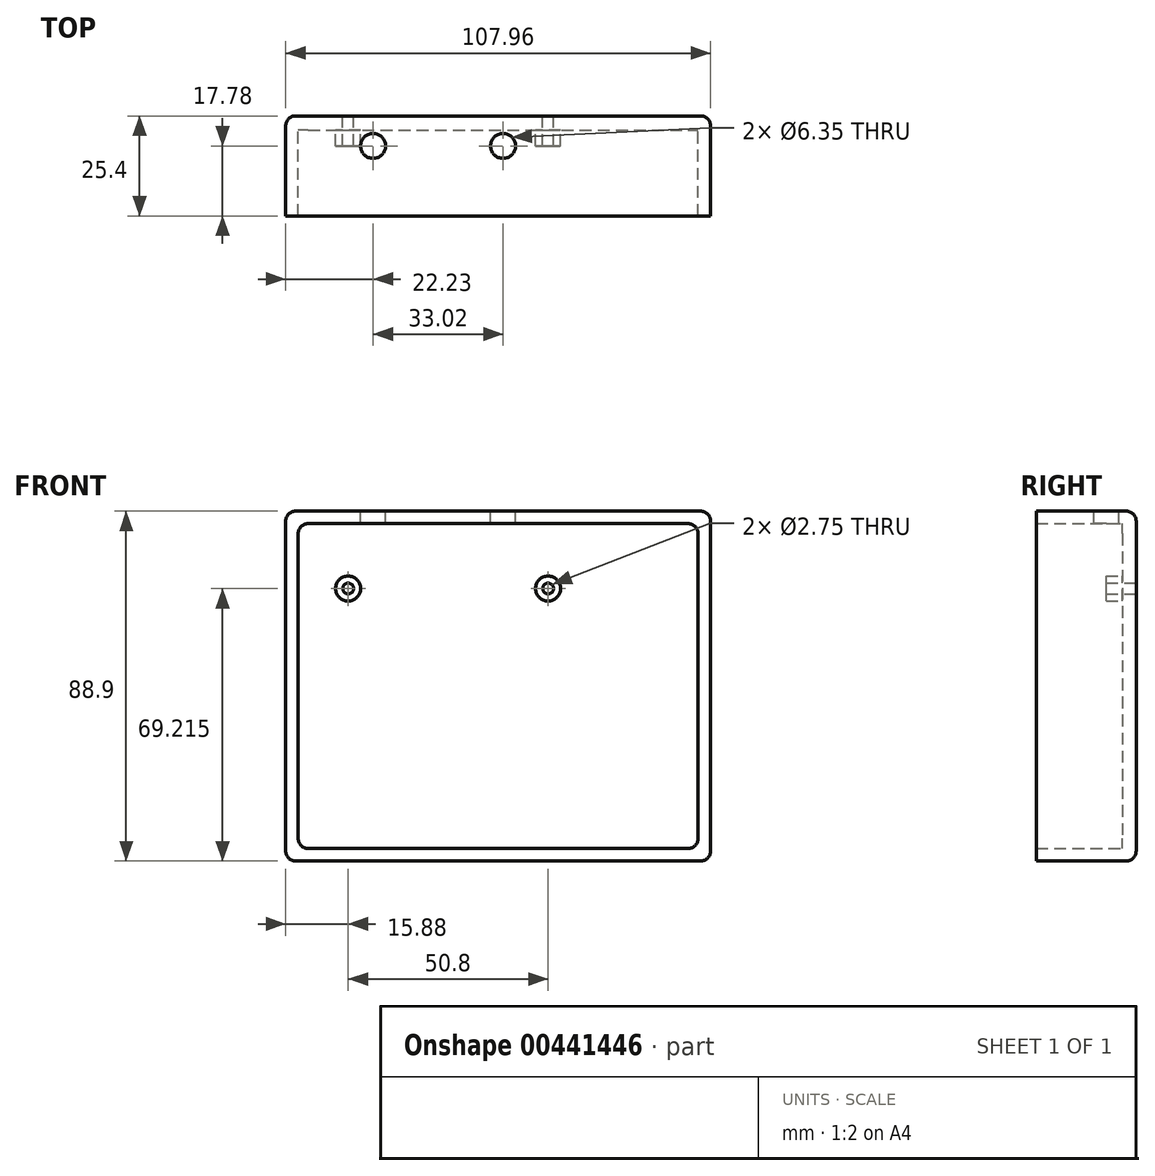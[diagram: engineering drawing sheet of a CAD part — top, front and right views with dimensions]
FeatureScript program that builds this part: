
annotation { "Feature Type Name" : "Feature", "Feature Type Description" : "" }
export const myFeature = defineFeature(function(context is Context, id is Id, definition is map)
    precondition{}
    {
        {
            var Q0;
            Q0=qCreatedBy(makeId("Front.planeOp"),FACE);
            var sketch = newSketch(context, id + "F0", { "sketchPlane" : qUnion([Q0])});
            skLineSegment(sketch, "E0.bottom", {"start": v(50.8, -41.27) * mm, "end": v(-50.8, -41.28) * mm});
            skLineSegment(sketch, "E0.top", {"start": v(50.8, 41.28) * mm, "end": v(-50.8, 41.27) * mm});
            skLineSegment(sketch, "E0.left", {"start": v(50.8, -41.27) * mm, "end": v(50.8, 41.28) * mm});
            skLineSegment(sketch, "E0.right", {"start": v(-50.8, -41.28) * mm, "end": v(-50.8, 41.27) * mm});
            skPoint(sketch, "E0.middle", {"position": v(0, 0) * mm});
            skCircle(sketch, "E1", {"center": v(-38.1, 24.77) * mm, "radius": 3.18 * mm});
            skCircle(sketch, "E2", {"center": v(-38.1, 24.77) * mm, "radius": 1.38 * mm});
            skCircle(sketch, "E3", {"center": v(12.7, 24.77) * mm, "radius": 3.18 * mm});
            skCircle(sketch, "E4", {"center": v(12.7, 24.77) * mm, "radius": 1.38 * mm});
            skLineSegment(sketch, "E5.bottom", {"start": v(53.98, -44.45) * mm, "end": v(-53.98, -44.45) * mm});
            skLineSegment(sketch, "E5.top", {"start": v(53.98, 44.45) * mm, "end": v(-53.98, 44.45) * mm});
            skLineSegment(sketch, "E5.left", {"start": v(53.98, -44.45) * mm, "end": v(53.98, 44.45) * mm});
            skLineSegment(sketch, "E5.right", {"start": v(-53.98, -44.45) * mm, "end": v(-53.98, 44.45) * mm});
            skSolve(sketch);
        }
        {
            var Q0;
            Q0=makeQuery(id+"F0.imprint","IMPRINT",FACE,{"disambiguationData":[TD([[makeQuery(id+"F0.imprint","IMPRINT",EDGE,{"derivedFrom":sQuery(id+"F0.wireOp",EDGE,"E0.bottom")}),1.0]])]});
            var Q1;
            Q1=makeQuery(id+"F0.imprint","IMPRINT",FACE,{"disambiguationData":[TD([[makeQuery(id+"F0.imprint","IMPRINT",EDGE,{"derivedFrom":sQuery(id+"F0.wireOp",EDGE,"E0.bottom")}),-1.0]])]});
            extrude(context, id + "F1", {"entities" : qUnion([Q0, Q1]), "depth" : 3.56 * mm});
        }
        {
            var Q0;
            Q0=makeQuery(id+"F0.imprint","IMPRINT",FACE,{"disambiguationData":[TD([[makeQuery(id+"F0.imprint","IMPRINT",EDGE,{"derivedFrom":sQuery(id+"F0.wireOp",EDGE,"E1")}),1.0]])]});
            var Q1;
            Q1=makeQuery(id+"F0.imprint","IMPRINT",FACE,{"disambiguationData":[TD([[makeQuery(id+"F0.imprint","IMPRINT",EDGE,{"derivedFrom":sQuery(id+"F0.wireOp",EDGE,"E3")}),1.0]])]});
            extrude(context, id + "F2", {"entities" : qUnion([Q0, Q1]), "operationType" : NewBodyOperationType.ADD, "depth" : 7.62 * mm});
        }
        {
            var Q0;
            Q0=makeQuery(id+"F0.imprint","IMPRINT",FACE,{"disambiguationData":[TD([[makeQuery(id+"F0.imprint","IMPRINT",EDGE,{"derivedFrom":sQuery(id+"F0.wireOp",EDGE,"E0.bottom")}),1.0]])]});
            extrude(context, id + "F3", {"entities" : qUnion([Q0]), "operationType" : NewBodyOperationType.ADD, "depth" : 25.4 * mm});
        }
        {
            var Q0;
            {var subQ0=sQuery(id+"F0.wireOp",EDGE,"E5.top");Q0=makeQuery(id+"F3.boolean.opBoolean","MERGE",FACE,{"derivedFrom":[makeQuery(id+"F1.opExtrude","SWEPT_FACE",FACE,{"disambiguationData":[OSD([subQ0])]}),makeQuery(id+"F3.opExtrude","SWEPT_FACE",FACE,{"disambiguationData":[OSD([subQ0])]})]});}
            var sketch = newSketch(context, id + "F4", { "sketchPlane" : qUnion([Q0])});
            skCircle(sketch, "E6", {"center": v(-31.75, -7.62) * mm, "radius": 3.18 * mm});
            skCircle(sketch, "E7", {"center": v(1.27, -7.62) * mm, "radius": 3.18 * mm});
            skSolve(sketch);
        }
        {
            var Q0;
            Q0=makeQuery(id+"F4.imprint","IMPRINT",FACE,{"disambiguationData":[TD([[makeQuery(id+"F4.imprint","IMPRINT",EDGE,{"derivedFrom":sQuery(id+"F4.wireOp",EDGE,"E7")}),1.0]])]});
            var Q1;
            Q1=makeQuery(id+"F4.imprint","IMPRINT",FACE,{"disambiguationData":[TD([[makeQuery(id+"F4.imprint","IMPRINT",EDGE,{"derivedFrom":sQuery(id+"F4.wireOp",EDGE,"E6")}),1.0]])]});
            extrude(context, id + "F5", {"entities" : qUnion([Q0, Q1]), "operationType" : NewBodyOperationType.REMOVE, "oppositeDirection" : true, "depth" : 5.08 * mm});
        }
        {
            var Q0;
            {var subQ0=sQuery(id+"F0.wireOp",EDGE,"E5.right");var subQ1=sQuery(id+"F0.wireOp",EDGE,"E5.top");Q0=makeQuery(id+"F3.boolean.opBoolean","MERGE",EDGE,{"derivedFrom":[makeQuery(id+"F1.opExtrude","SWEPT_EDGE",EDGE,{"disambiguationData":[OSD([subQ1,subQ0])]}),makeQuery(id+"F3.opExtrude","SWEPT_EDGE",EDGE,{"disambiguationData":[OSD([subQ1,subQ0])]})]});}
            var Q1;
            Q1=makeQuery(id+"F3.opExtrude","SWEPT_EDGE",EDGE,{"disambiguationData":[OSD([sQuery(id+"F0.wireOp",EDGE,"E0.top"),sQuery(id+"F0.wireOp",EDGE,"E0.right")])]});
            var Q2;
            {var subQ0=sQuery(id+"F0.wireOp",EDGE,"E5.left");var subQ1=sQuery(id+"F0.wireOp",EDGE,"E5.top");Q2=makeQuery(id+"F3.boolean.opBoolean","MERGE",EDGE,{"derivedFrom":[makeQuery(id+"F1.opExtrude","SWEPT_EDGE",EDGE,{"disambiguationData":[OSD([subQ1,subQ0])]}),makeQuery(id+"F3.opExtrude","SWEPT_EDGE",EDGE,{"disambiguationData":[OSD([subQ1,subQ0])]})]});}
            var Q3;
            {var subQ0=sQuery(id+"F0.wireOp",EDGE,"E5.right");var subQ1=sQuery(id+"F0.wireOp",EDGE,"E5.bottom");Q3=makeQuery(id+"F3.boolean.opBoolean","MERGE",EDGE,{"derivedFrom":[makeQuery(id+"F1.opExtrude","SWEPT_EDGE",EDGE,{"disambiguationData":[OSD([subQ1,subQ0])]}),makeQuery(id+"F3.opExtrude","SWEPT_EDGE",EDGE,{"disambiguationData":[OSD([subQ1,subQ0])]})]});}
            var Q4;
            Q4=makeQuery(id+"F3.opExtrude","SWEPT_EDGE",EDGE,{"disambiguationData":[OSD([sQuery(id+"F0.wireOp",EDGE,"E0.top"),sQuery(id+"F0.wireOp",EDGE,"E0.left")])]});
            var Q5;
            Q5=makeQuery(id+"F3.opExtrude","SWEPT_EDGE",EDGE,{"disambiguationData":[OSD([sQuery(id+"F0.wireOp",EDGE,"E0.bottom"),sQuery(id+"F0.wireOp",EDGE,"E0.right")])]});
            var Q6;
            {var subQ0=sQuery(id+"F0.wireOp",EDGE,"E5.left");var subQ1=sQuery(id+"F0.wireOp",EDGE,"E5.bottom");Q6=makeQuery(id+"F3.boolean.opBoolean","MERGE",EDGE,{"derivedFrom":[makeQuery(id+"F1.opExtrude","SWEPT_EDGE",EDGE,{"disambiguationData":[OSD([subQ1,subQ0])]}),makeQuery(id+"F3.opExtrude","SWEPT_EDGE",EDGE,{"disambiguationData":[OSD([subQ1,subQ0])]})]});}
            var Q7;
            Q7=makeQuery(id+"F3.opExtrude","SWEPT_EDGE",EDGE,{"disambiguationData":[OSD([sQuery(id+"F0.wireOp",EDGE,"E0.bottom"),sQuery(id+"F0.wireOp",EDGE,"E0.left")])]});
            var Q8;
            Q8=makeQuery(id+"F1.opExtrude","CAP_EDGE",EDGE,{"disambiguationData":[OSD([sQuery(id+"F0.wireOp",EDGE,"E5.bottom")])],"isStart":true});
            var Q9;
            Q9=makeQuery(id+"F1.opExtrude","CAP_EDGE",EDGE,{"disambiguationData":[OSD([sQuery(id+"F0.wireOp",EDGE,"E5.left")])],"isStart":true});
            var Q10;
            Q10=makeQuery(id+"F1.opExtrude","CAP_EDGE",EDGE,{"disambiguationData":[OSD([sQuery(id+"F0.wireOp",EDGE,"E5.right")])],"isStart":true});
            var Q11;
            Q11=makeQuery(id+"F1.opExtrude","CAP_EDGE",EDGE,{"disambiguationData":[OSD([sQuery(id+"F0.wireOp",EDGE,"E5.top")])],"isStart":true});
            var Q12;
            Q12=makeQuery(id+"F1.opExtrude","CAP_EDGE",EDGE,{"disambiguationData":[OSD([sQuery(id+"F0.wireOp",EDGE,"E3")])],"isStart":false});
            var Q13;
            Q13=makeQuery(id+"F1.opExtrude","CAP_EDGE",EDGE,{"disambiguationData":[OSD([sQuery(id+"F0.wireOp",EDGE,"E1")])],"isStart":false});
            fillet(context, id + "F6", {"entities" : qUnion([Q0, Q1, Q2, Q3, Q4, Q5, Q6, Q7, Q8, Q9, Q10, Q11, Q12, Q13]), "radius" : 2.54 * mm, "tangentPropagation" : true, "allowEdgeOverflow" : false});
        }
    });
